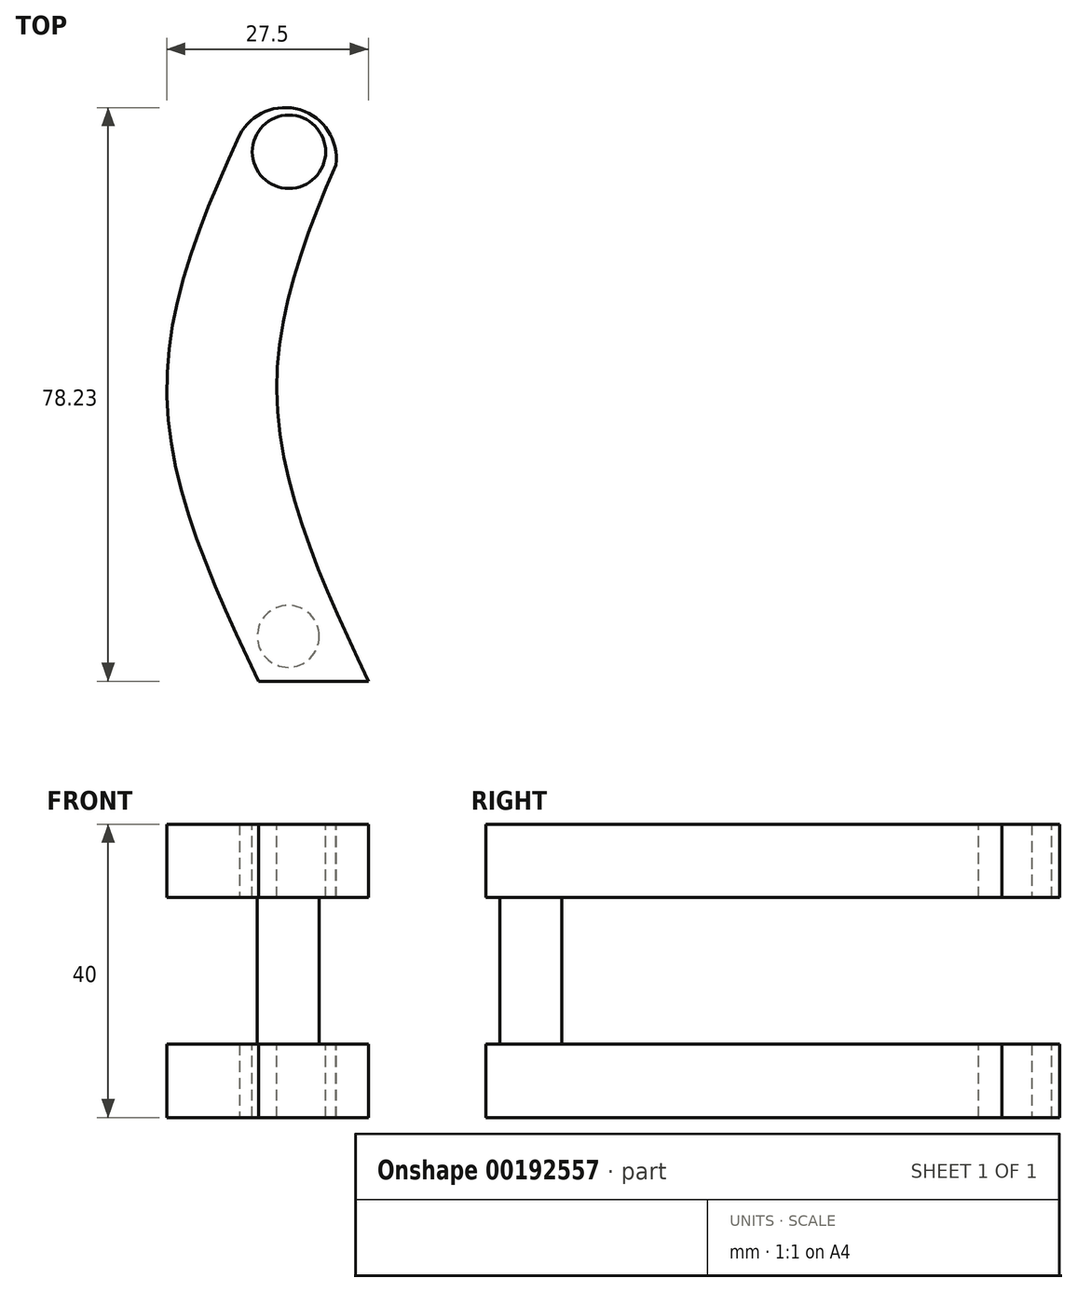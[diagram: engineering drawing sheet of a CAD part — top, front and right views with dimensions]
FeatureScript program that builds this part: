
annotation { "Feature Type Name" : "Feature", "Feature Type Description" : "" }
export const myFeature = defineFeature(function(context is Context, id is Id, definition is map)
    precondition{}
    {
        {
            var Q0;
            Q0=qCreatedBy(makeId("Front.planeOp"),FACE);
            var sketch = newSketch(context, id + "F0", { "sketchPlane" : qUnion([Q0])});
            skLineSegment(sketch, "E0.bottom", {"start": v(7.5, 10) * mm, "end": v(-7.5, 10) * mm});
            skLineSegment(sketch, "E0.top", {"start": v(7.5, 20) * mm, "end": v(-7.5, 20) * mm});
            skLineSegment(sketch, "E0.left", {"start": v(7.5, 10) * mm, "end": v(7.5, 20) * mm});
            skLineSegment(sketch, "E0.right", {"start": v(-7.5, 10) * mm, "end": v(-7.5, 20) * mm});
            skPoint(sketch, "E0.middle", {"position": v(0, 15) * mm});
            skLineSegment(sketch, "E1.bottom", {"start": v(7.5, -20) * mm, "end": v(-7.5, -20) * mm});
            skLineSegment(sketch, "E1.top", {"start": v(7.5, -10) * mm, "end": v(-7.5, -10) * mm});
            skLineSegment(sketch, "E1.left", {"start": v(7.5, -20) * mm, "end": v(7.5, -10) * mm});
            skLineSegment(sketch, "E1.right", {"start": v(-7.5, -20) * mm, "end": v(-7.5, -10) * mm});
            skPoint(sketch, "E1.middle", {"position": v(0, -15) * mm});
            skSolve(sketch);
        }
        {
            var Q0;
            Q0=qCreatedBy(makeId("Front.planeOp"),FACE);
            cPlane(context, id + "F1", {"entities" : qUnion([Q0]), "cplaneType" : CPlaneType.OFFSET, "offset" : 40 * mm, "width" : 150 * mm, "height" : 150 * mm});
        }
        {
            var Q0;
            Q0=qCreatedBy(id+"F1.planeOp",FACE);
            var sketch = newSketch(context, id + "F2", { "sketchPlane" : qUnion([Q0])});
            skLineSegment(sketch, "E2.bottom", {"start": v(-20, 10) * mm, "end": v(-5, 10) * mm});
            skLineSegment(sketch, "E2.top", {"start": v(-20, 20) * mm, "end": v(-5, 20) * mm});
            skLineSegment(sketch, "E2.left", {"start": v(-20, 10) * mm, "end": v(-20, 20) * mm});
            skLineSegment(sketch, "E2.right", {"start": v(-5, 10) * mm, "end": v(-5, 20) * mm});
            skPoint(sketch, "E2.middle", {"position": v(-12.5, 15) * mm});
            skLineSegment(sketch, "E3.bottom", {"start": v(-5, -20) * mm, "end": v(-20, -20) * mm});
            skLineSegment(sketch, "E3.top", {"start": v(-5, -10) * mm, "end": v(-20, -10) * mm});
            skLineSegment(sketch, "E3.left", {"start": v(-5, -20) * mm, "end": v(-5, -10) * mm});
            skLineSegment(sketch, "E3.right", {"start": v(-20, -20) * mm, "end": v(-20, -10) * mm});
            skPoint(sketch, "E3.middle", {"position": v(-12.5, -15) * mm});
            skSolve(sketch);
        }
        {
            var Q0;
            Q0=qCreatedBy(id+"F1.planeOp",FACE);
            cPlane(context, id + "F3", {"entities" : qUnion([Q0]), "cplaneType" : CPlaneType.OFFSET, "offset" : 40 * mm, "width" : 150 * mm, "height" : 150 * mm});
        }
        {
            var Q0;
            Q0=qCreatedBy(id+"F3.planeOp",FACE);
            var sketch = newSketch(context, id + "F4", { "sketchPlane" : qUnion([Q0])});
            skLineSegment(sketch, "E4.bottom", {"start": v(7.5, 10) * mm, "end": v(-7.5, 10) * mm});
            skLineSegment(sketch, "E4.top", {"start": v(7.5, 20) * mm, "end": v(-7.5, 20) * mm});
            skLineSegment(sketch, "E4.left", {"start": v(7.5, 10) * mm, "end": v(7.5, 20) * mm});
            skLineSegment(sketch, "E4.right", {"start": v(-7.5, 10) * mm, "end": v(-7.5, 20) * mm});
            skPoint(sketch, "E4.middle", {"position": v(0, 15) * mm});
            skLineSegment(sketch, "E5.bottom", {"start": v(7.5, -20) * mm, "end": v(-7.5, -20) * mm});
            skLineSegment(sketch, "E5.top", {"start": v(7.5, -10) * mm, "end": v(-7.5, -10) * mm});
            skLineSegment(sketch, "E5.left", {"start": v(7.5, -20) * mm, "end": v(7.5, -10) * mm});
            skLineSegment(sketch, "E5.right", {"start": v(-7.5, -20) * mm, "end": v(-7.5, -10) * mm});
            skPoint(sketch, "E5.middle", {"position": v(0, -15) * mm});
            skSolve(sketch);
        }
        {
            var Q0;
            Q0=makeQuery(id+"F4.imprint","IMPRINT",FACE,{"disambiguationData":[TD([[makeQuery(id+"F4.imprint","IMPRINT",EDGE,{"derivedFrom":sQuery(id+"F4.wireOp",EDGE,"E4.bottom")}),-1.0]])]});
            var Q1;
            Q1=makeQuery(id+"F2.imprint","IMPRINT",FACE,{"disambiguationData":[TD([[makeQuery(id+"F2.imprint","IMPRINT",EDGE,{"derivedFrom":sQuery(id+"F2.wireOp",EDGE,"E2.bottom")}),1.0]])]});
            var Q2;
            Q2=makeQuery(id+"F0.imprint","IMPRINT",FACE,{"disambiguationData":[TD([[makeQuery(id+"F0.imprint","IMPRINT",EDGE,{"derivedFrom":sQuery(id+"F0.wireOp",EDGE,"E0.bottom")}),-1.0]])]});
            loft(context, id + "F5", {"sheetProfilesArray" : [{ "sheetProfileEntities" : qUnion([Q0]) }, { "sheetProfileEntities" : qUnion([Q1]) }, { "sheetProfileEntities" : qUnion([Q2]) }]});
        }
        {
            var Q0;
            Q0=makeQuery(id+"F4.imprint","IMPRINT",FACE,{"disambiguationData":[TD([[makeQuery(id+"F4.imprint","IMPRINT",EDGE,{"derivedFrom":sQuery(id+"F4.wireOp",EDGE,"E5.bottom")}),-1.0]])]});
            var Q1;
            Q1=makeQuery(id+"F2.imprint","IMPRINT",FACE,{"disambiguationData":[TD([[makeQuery(id+"F2.imprint","IMPRINT",EDGE,{"derivedFrom":sQuery(id+"F2.wireOp",EDGE,"E3.bottom")}),-1.0]])]});
            var Q2;
            Q2=makeQuery(id+"F0.imprint","IMPRINT",FACE,{"disambiguationData":[TD([[makeQuery(id+"F0.imprint","IMPRINT",EDGE,{"derivedFrom":sQuery(id+"F0.wireOp",EDGE,"E1.bottom")}),-1.0]])]});
            loft(context, id + "F6", {"sheetProfilesArray" : [{ "sheetProfileEntities" : qUnion([Q0]) }, { "sheetProfileEntities" : qUnion([Q1]) }, { "sheetProfileEntities" : qUnion([Q2]) }]});
        }
        {
            var Q0;
            Q0=makeQuery(id+"F5.opLoft","SWEPT_FACE",FACE,{"disambiguationData":[OSD([sQuery(id+"F2.wireOp",EDGE,"E2.top"),sQuery(id+"F2.wireOp",EDGE,"E2.left"),sQuery(id+"F2.wireOp",EDGE,"E2.right"),sQuery(id+"F4.wireOp",EDGE,"E4.top"),sQuery(id+"F4.wireOp",EDGE,"E4.left"),sQuery(id+"F4.wireOp",EDGE,"E4.right")])]});
            var sketch = newSketch(context, id + "F7", { "sketchPlane" : qUnion([Q0])});
            skCircle(sketch, "E6", {"center": v(-3.43, -73.88) * mm, "radius": 4.22 * mm});
            skSolve(sketch);
        }
        {
            var Q0;
            Q0=qSketchRegion(id+"F7",true);
            extrude(context, id + "F8", {"entities" : qUnion([Q0]), "operationType" : NewBodyOperationType.ADD, "oppositeDirection" : true, "depth" : 35 * mm});
        }
        {
            var Q0;
            Q0=makeQuery(id+"F5.opLoft","SWEPT_FACE",FACE,{"disambiguationData":[OSD([sQuery(id+"F2.wireOp",EDGE,"E2.top"),sQuery(id+"F2.wireOp",EDGE,"E2.left"),sQuery(id+"F2.wireOp",EDGE,"E2.right"),sQuery(id+"F4.wireOp",EDGE,"E4.top"),sQuery(id+"F4.wireOp",EDGE,"E4.left"),sQuery(id+"F4.wireOp",EDGE,"E4.right")])]});
            var sketch = newSketch(context, id + "F9", { "sketchPlane" : qUnion([Q0])});
            skCircle(sketch, "E7", {"center": v(-3.33, -7.8) * mm, "radius": 5 * mm});
            skSolve(sketch);
        }
        {
            var Q0;
            Q0=qSketchRegion(id+"F9",true);
            extrude(context, id + "F10", {"entities" : qUnion([Q0]), "operationType" : NewBodyOperationType.REMOVE, "oppositeDirection" : true, "depth" : 50 * mm});
        }
        {
            var Q0;
            Q0=makeQuery(id+"F5.opLoft","SWEPT_FACE",FACE,{"disambiguationData":[OSD([sQuery(id+"F2.wireOp",EDGE,"E2.top"),sQuery(id+"F2.wireOp",EDGE,"E2.left"),sQuery(id+"F2.wireOp",EDGE,"E2.right"),sQuery(id+"F4.wireOp",EDGE,"E4.top"),sQuery(id+"F4.wireOp",EDGE,"E4.left"),sQuery(id+"F4.wireOp",EDGE,"E4.right")])]});
            var sketch = newSketch(context, id + "F11", { "sketchPlane" : qUnion([Q0])});
            skArc(sketch, "E8", {"start": v(3.09, -9.6) * mm, "mid": v(-2.1, -2) * mm, "end": v(-10.34, -6.1) * mm});
            skLineSegment(sketch, "E9", {"start": v(-10.34, -6.1) * mm, "end": v(-7.5, 0) * mm});
            skLineSegment(sketch, "E10", {"start": v(-7.5, 0) * mm, "end": v(7.5, 0) * mm});
            skLineSegment(sketch, "E11", {"start": v(7.5, 0) * mm, "end": v(3.09, -9.6) * mm});
            skSolve(sketch);
        }
        {
            var Q0;
            Q0 = qSketchRegion(id + "F11", true);
            extrude(context, id + "F12", {"entities" : qUnion([Q0]), "operationType" : NewBodyOperationType.REMOVE, "endBound" : BoundingType.THROUGH_ALL, "oppositeDirection" : true, "depth" : 25 * mm});
        }
    });
